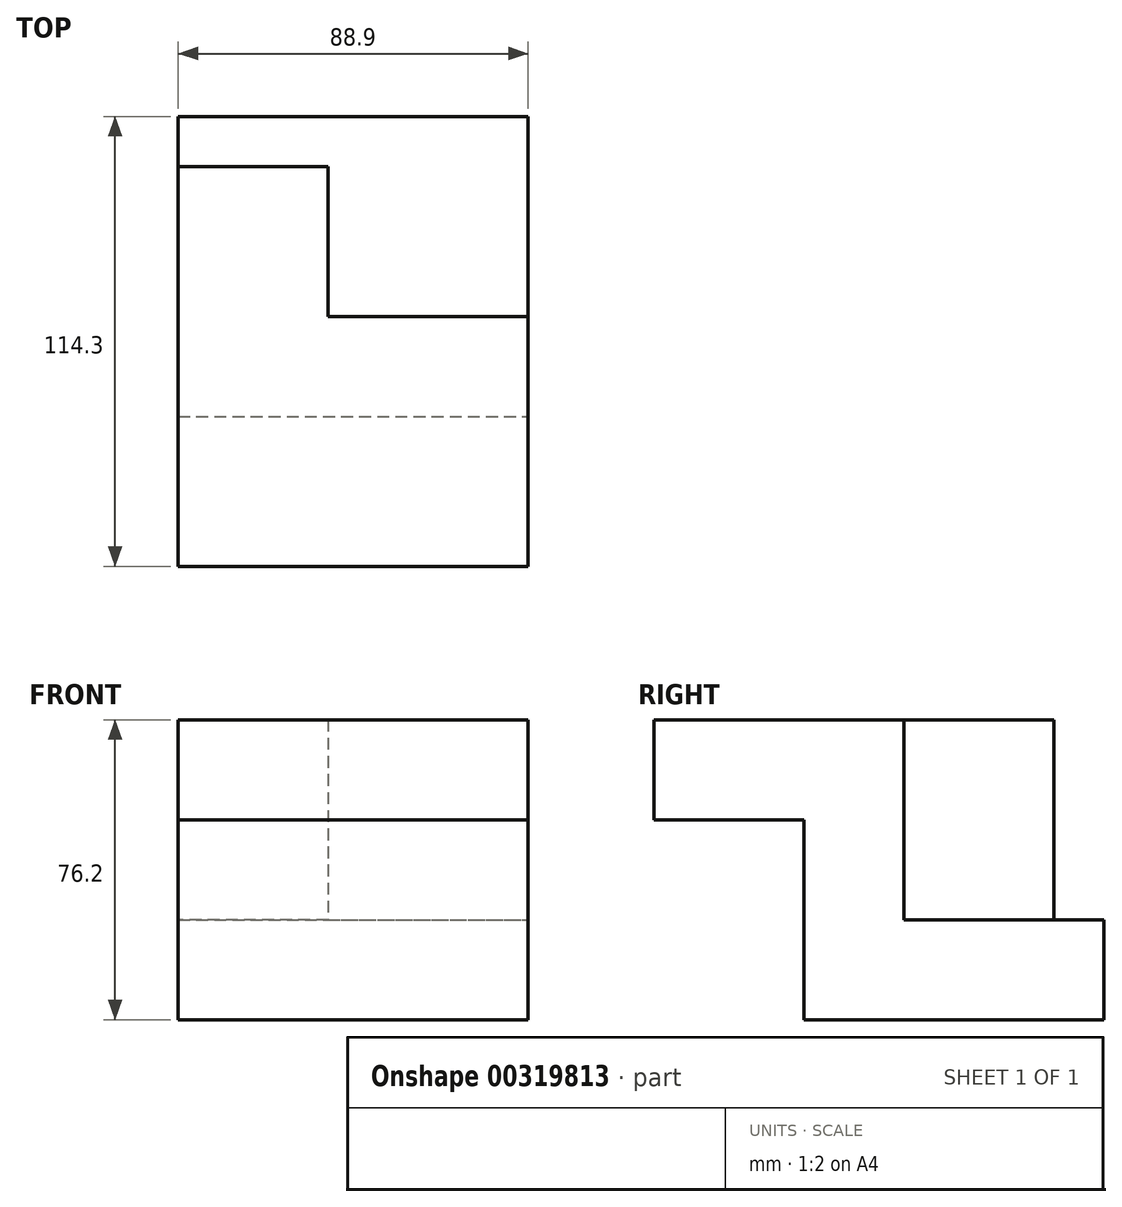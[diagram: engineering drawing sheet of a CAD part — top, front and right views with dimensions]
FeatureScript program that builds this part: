
annotation { "Feature Type Name" : "Feature", "Feature Type Description" : "" }
export const myFeature = defineFeature(function(context is Context, id is Id, definition is map)
    precondition{}
    {
        {
            var Q0;
            Q0=qCreatedBy(makeId("Right.planeOp"),FACE);
            var sketch = newSketch(context, id + "F0", { "sketchPlane" : qUnion([Q0])});
            skLineSegment(sketch, "E0", {"start": v(-74.47, 35.85) * mm, "end": v(-10.97, 35.85) * mm});
            skLineSegment(sketch, "E1", {"start": v(-10.97, 35.85) * mm, "end": v(-10.97, -14.95) * mm});
            skLineSegment(sketch, "E2", {"start": v(-10.97, -14.95) * mm, "end": v(39.83, -14.95) * mm});
            skLineSegment(sketch, "E3", {"start": v(39.83, -14.95) * mm, "end": v(39.83, -40.35) * mm});
            skLineSegment(sketch, "E4", {"start": v(39.83, -40.35) * mm, "end": v(-36.37, -40.35) * mm});
            skLineSegment(sketch, "E5", {"start": v(-36.37, -40.35) * mm, "end": v(-36.37, 10.45) * mm});
            skLineSegment(sketch, "E6", {"start": v(-36.37, 10.45) * mm, "end": v(-74.47, 10.45) * mm});
            skLineSegment(sketch, "E7", {"start": v(-74.47, 10.45) * mm, "end": v(-74.47, 35.85) * mm});
            skSolve(sketch);
        }
        {
            var Q0;
            Q0=makeQuery(id+"F0.imprint","IMPRINT",FACE,{"disambiguationData":[TD([[makeQuery(id+"F0.imprint","IMPRINT",EDGE,{"derivedFrom":sQuery(id+"F0.wireOp",EDGE,"E0")}),-1.0]])]});
            extrude(context, id + "F1", {"entities" : qUnion([Q0]), "oppositeDirection" : true, "depth" : 88.9 * mm});
        }
        {
            var Q0;
            Q0=makeQuery(id+"F1.opExtrude","CAP_FACE",FACE,{"disambiguationData":[OSD([sQuery(id+"F0.wireOp",EDGE,"E0"),sQuery(id+"F0.wireOp",EDGE,"E1"),sQuery(id+"F0.wireOp",EDGE,"E2"),sQuery(id+"F0.wireOp",EDGE,"E3"),sQuery(id+"F0.wireOp",EDGE,"E4"),sQuery(id+"F0.wireOp",EDGE,"E5"),sQuery(id+"F0.wireOp",EDGE,"E6"),sQuery(id+"F0.wireOp",EDGE,"E7")])],"isStart":false});
            var sketch = newSketch(context, id + "F2", { "sketchPlane" : qUnion([Q0])});
            skLineSegment(sketch, "E8", {"start": v(10.97, 35.85) * mm, "end": v(-27.13, 35.85) * mm});
            skLineSegment(sketch, "E9", {"start": v(-27.13, 35.85) * mm, "end": v(-27.13, -14.95) * mm});
            skSolve(sketch);
        }
        {
            var Q0;
            Q0=makeQuery(id+"F2.imprint","IMPRINT",FACE,{"disambiguationData":[TD([[makeQuery(id+"F2.imprint","IMPRINT",EDGE,{"derivedFrom":sQuery(id+"F2.wireOp",EDGE,"E8")}),1.0]])]});
            extrude(context, id + "F3", {"entities" : qUnion([Q0]), "operationType" : NewBodyOperationType.ADD, "oppositeDirection" : true, "depth" : 38.1 * mm});
        }
    });
